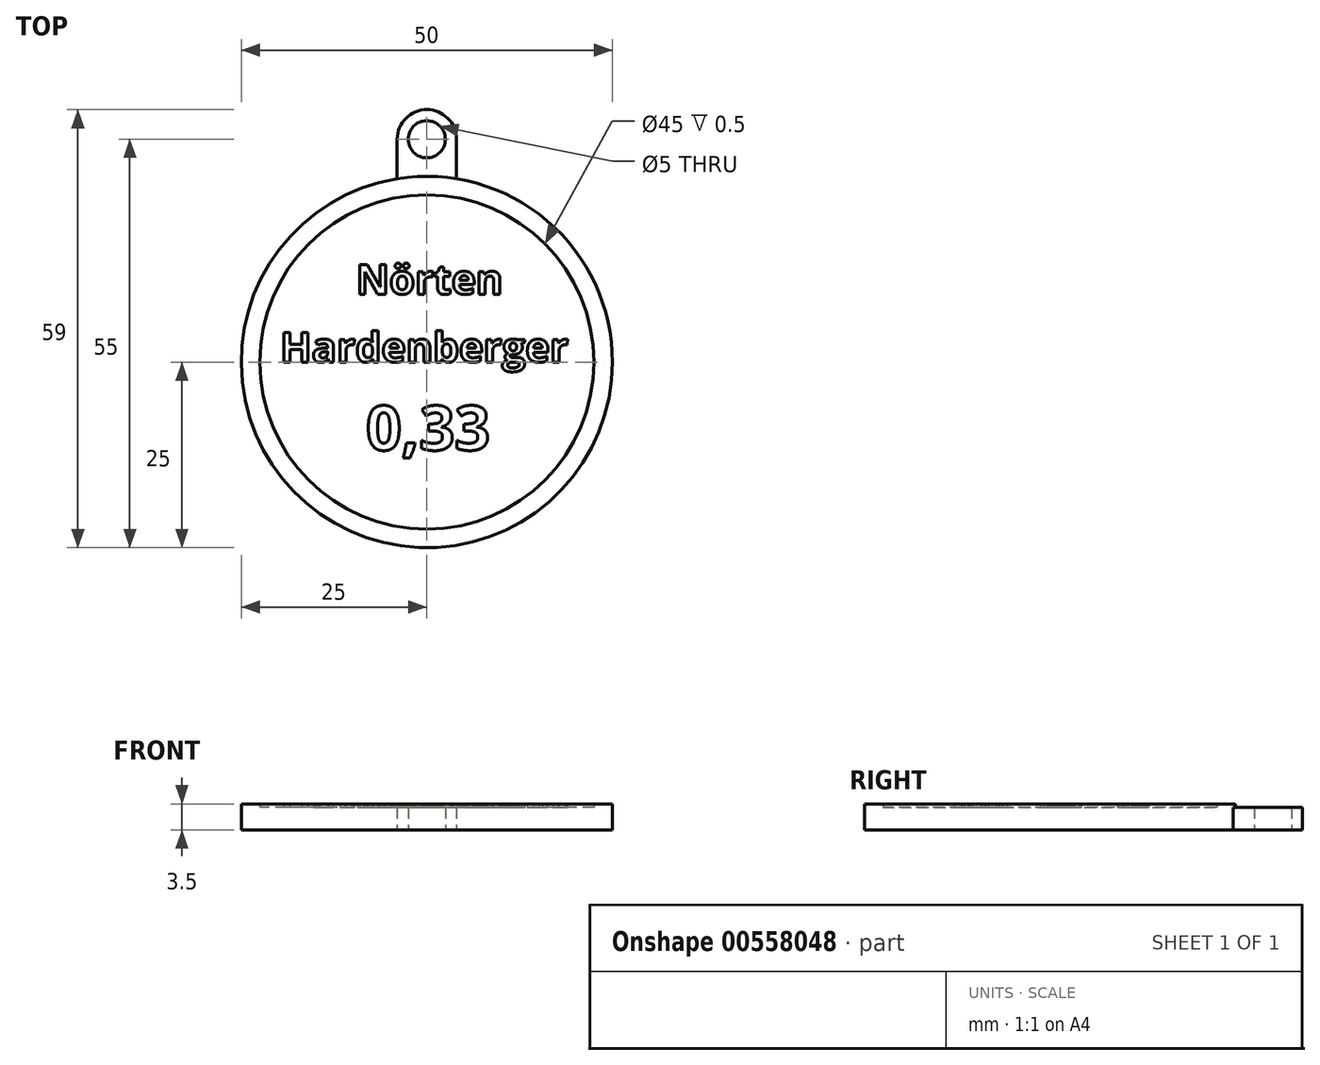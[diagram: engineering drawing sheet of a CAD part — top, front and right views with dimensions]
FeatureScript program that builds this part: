
annotation { "Feature Type Name" : "Feature", "Feature Type Description" : "" }
export const myFeature = defineFeature(function(context is Context, id is Id, definition is map)
    precondition{}
    {
        {
            var Q0;
            Q0=qCreatedBy(makeId("Top.planeOp"),FACE);
            var sketch = newSketch(context, id + "F0", { "sketchPlane" : qUnion([Q0])});
            skCircle(sketch, "E0", {"center": v(0, 0) * mm, "radius": 25 * mm});
            skCircle(sketch, "E1", {"center": v(0, 30) * mm, "radius": 2.5 * mm});
            skCircle(sketch, "E2", {"center": v(0, 30) * mm, "radius": 4 * mm});
            skLineSegment(sketch, "E3", {"start": v(-4, 30) * mm, "end": v(-4, 24.68) * mm});
            skLineSegment(sketch, "E4", {"start": v(4, 30) * mm, "end": v(4, 24.68) * mm});
            skCircle(sketch, "E5", {"center": v(0, 0) * mm, "radius": 22.5 * mm});
            skSolve(sketch);
        }
        {
            var Q0;
            {var subQ0=sQuery(id+"F0.wireOp",EDGE,"E0");var subQ1=makeQuery(id+"F0.imprint","INTERSECT",VERTEX,{"derivedFrom":[subQ0,sQuery(id+"F0.wireOp",EDGE,"E3")]});Q0=makeQuery(id+"F0.imprint","IMPRINT",FACE,{"disambiguationData":[TD([[makeQuery(id+"F0.imprint","IMPRINT",EDGE,{"disambiguationData":[TD([[subQ1,1.0]])],"derivedFrom":subQ0}),1.0]])]});}
            var Q1;
            {var subQ0=sQuery(id+"F0.wireOp",EDGE,"E3");Q1=makeQuery(id+"F0.imprint","IMPRINT",FACE,{"disambiguationData":[TD([[makeQuery(id+"F0.imprint","IMPRINT",EDGE,{"derivedFrom":subQ0}),1.0]])]});}
            var Q2;
            Q2=makeQuery(id+"F0.imprint","IMPRINT",FACE,{"disambiguationData":[TD([[makeQuery(id+"F0.imprint","IMPRINT",EDGE,{"derivedFrom":sQuery(id+"F0.wireOp",EDGE,"E1")}),-1.0]])]});
            var Q3;
            Q3=makeQuery(id+"F0.imprint","IMPRINT",FACE,{"disambiguationData":[TD([[makeQuery(id+"F0.imprint","IMPRINT",EDGE,{"derivedFrom":sQuery(id+"F0.wireOp",EDGE,"E5")}),1.0]])]});
            extrude(context, id + "F1", {"entities" : qUnion([Q0, Q1, Q2, Q3]), "depth" : 3 * mm, "offsetDistance" : 25 * mm});
        }
        {
            var Q0;
            Q0=makeQuery(id+"F1.opExtrude","CAP_FACE",FACE,{"disambiguationData":[OSD([sQuery(id+"F0.wireOp",EDGE,"E0"),sQuery(id+"F0.wireOp",EDGE,"E1"),sQuery(id+"F0.wireOp",EDGE,"E2"),sQuery(id+"F0.wireOp",EDGE,"E3"),sQuery(id+"F0.wireOp",EDGE,"E4")])],"isStart":false});
            var sketch = newSketch(context, id + "F2", { "sketchPlane" : qUnion([Q0])});
            skCircle(sketch, "E6", {"center": v(0, 0) * mm, "radius": 22.5 * mm});
            skText(sketch, "E7", { "text": "Nörten ", "fontName": "OpenSans-Bold.ttf"});
            skText(sketch, "E8", { "text": "Hardenberger", "fontName": "OpenSans-Bold.ttf"});
            skText(sketch, "E9", { "text": "0,33", "fontName": "OpenSans-Bold.ttf"});
            const initialGuessF2  = {"E7": [-0.00956, 0.00914, 1, 0, 0.004], "E8": [-0.01975, 0, 1, 0, 0.004], "E9": [-0.00818, -0.01186, 1, 0, 0.006]};
            skSetInitialGuess(sketch, initialGuessF2);
            skSolve(sketch);
        }
        {
            var Q0;
            Q0=makeQuery(id+"F2.imprint","IMPRINT",FACE,{"disambiguationData":[TD([[makeQuery(id+"F2.imprint","IMPRINT",EDGE,{"derivedFrom":sQuery(id+"F2.wireOp",EDGE,"E8.sketch_text.stroke-0")}),-1.0]])]});
            var Q1;
            Q1=makeQuery(id+"F2.imprint","IMPRINT",FACE,{"disambiguationData":[TD([[makeQuery(id+"F2.imprint","IMPRINT",EDGE,{"derivedFrom":sQuery(id+"F2.wireOp",EDGE,"E8.sketch_text.stroke-12")}),-1.0]])]});
            var Q2;
            Q2=makeQuery(id+"F2.imprint","IMPRINT",FACE,{"disambiguationData":[TD([[makeQuery(id+"F2.imprint","IMPRINT",EDGE,{"derivedFrom":sQuery(id+"F2.wireOp",EDGE,"E8.sketch_text.stroke-37")}),-1.0]])]});
            var Q3;
            Q3=makeQuery(id+"F2.imprint","IMPRINT",FACE,{"disambiguationData":[TD([[makeQuery(id+"F2.imprint","IMPRINT",EDGE,{"derivedFrom":sQuery(id+"F2.wireOp",EDGE,"E8.sketch_text.stroke-50")}),-1.0]])]});
            var Q4;
            Q4=makeQuery(id+"F2.imprint","IMPRINT",FACE,{"disambiguationData":[TD([[makeQuery(id+"F2.imprint","IMPRINT",EDGE,{"derivedFrom":sQuery(id+"F2.wireOp",EDGE,"E8.sketch_text.stroke-73")}),-1.0]])]});
            var Q5;
            Q5=makeQuery(id+"F2.imprint","IMPRINT",FACE,{"disambiguationData":[TD([[makeQuery(id+"F2.imprint","IMPRINT",EDGE,{"derivedFrom":sQuery(id+"F2.wireOp",EDGE,"E8.sketch_text.stroke-93")}),-1.0]])]});
            var Q6;
            Q6=makeQuery(id+"F2.imprint","IMPRINT",FACE,{"disambiguationData":[TD([[makeQuery(id+"F2.imprint","IMPRINT",EDGE,{"derivedFrom":sQuery(id+"F2.wireOp",EDGE,"E8.sketch_text.stroke-110")}),-1.0]])]});
            var Q7;
            Q7=makeQuery(id+"F2.imprint","IMPRINT",FACE,{"disambiguationData":[TD([[makeQuery(id+"F2.imprint","IMPRINT",EDGE,{"derivedFrom":sQuery(id+"F2.wireOp",EDGE,"E8.sketch_text.stroke-133")}),-1.0]])]});
            var Q8;
            Q8=makeQuery(id+"F2.imprint","IMPRINT",FACE,{"disambiguationData":[TD([[makeQuery(id+"F2.imprint","IMPRINT",EDGE,{"derivedFrom":sQuery(id+"F2.wireOp",EDGE,"E8.sketch_text.stroke-153")}),-1.0]])]});
            var Q9;
            Q9=makeQuery(id+"F2.imprint","IMPRINT",FACE,{"disambiguationData":[TD([[makeQuery(id+"F2.imprint","IMPRINT",EDGE,{"derivedFrom":sQuery(id+"F2.wireOp",EDGE,"E8.sketch_text.stroke-166")}),-1.0]])]});
            var Q10;
            Q10=makeQuery(id+"F2.imprint","IMPRINT",FACE,{"disambiguationData":[TD([[makeQuery(id+"F2.imprint","IMPRINT",EDGE,{"derivedFrom":sQuery(id+"F2.wireOp",EDGE,"E8.sketch_text.stroke-210")}),-1.0]])]});
            var Q11;
            Q11=makeQuery(id+"F2.imprint","IMPRINT",FACE,{"disambiguationData":[TD([[makeQuery(id+"F2.imprint","IMPRINT",EDGE,{"derivedFrom":sQuery(id+"F2.wireOp",EDGE,"E8.sketch_text.stroke-230")}),-1.0]])]});
            var Q12;
            Q12=makeQuery(id+"F2.imprint","IMPRINT",FACE,{"disambiguationData":[TD([[makeQuery(id+"F2.imprint","IMPRINT",EDGE,{"derivedFrom":sQuery(id+"F2.wireOp",EDGE,"E9.sketch_text.stroke-21")}),-1.0]])]});
            var Q13;
            Q13=makeQuery(id+"F2.imprint","IMPRINT",FACE,{"disambiguationData":[TD([[makeQuery(id+"F2.imprint","IMPRINT",EDGE,{"derivedFrom":sQuery(id+"F2.wireOp",EDGE,"E9.sketch_text.stroke-0")}),-1.0]])]});
            var Q14;
            Q14=makeQuery(id+"F2.imprint","IMPRINT",FACE,{"disambiguationData":[TD([[makeQuery(id+"F2.imprint","IMPRINT",EDGE,{"derivedFrom":sQuery(id+"F2.wireOp",EDGE,"E9.sketch_text.stroke-48")}),-1.0]])]});
            var Q15;
            Q15=makeQuery(id+"F2.imprint","IMPRINT",FACE,{"disambiguationData":[TD([[makeQuery(id+"F2.imprint","IMPRINT",EDGE,{"derivedFrom":sQuery(id+"F2.wireOp",EDGE,"E7.sketch_text.stroke-14")}),-1.0]])]});
            var Q16;
            Q16=makeQuery(id+"F2.imprint","IMPRINT",FACE,{"disambiguationData":[TD([[makeQuery(id+"F2.imprint","IMPRINT",EDGE,{"derivedFrom":sQuery(id+"F2.wireOp",EDGE,"E7.sketch_text.stroke-0")}),-1.0]])]});
            var Q17;
            Q17=makeQuery(id+"F2.imprint","IMPRINT",FACE,{"disambiguationData":[TD([[makeQuery(id+"F2.imprint","IMPRINT",EDGE,{"derivedFrom":sQuery(id+"F2.wireOp",EDGE,"E7.sketch_text.stroke-48")}),-1.0]])]});
            var Q18;
            Q18=makeQuery(id+"F2.imprint","IMPRINT",FACE,{"disambiguationData":[TD([[makeQuery(id+"F2.imprint","IMPRINT",EDGE,{"derivedFrom":sQuery(id+"F2.wireOp",EDGE,"E7.sketch_text.stroke-61")}),-1.0]])]});
            var Q19;
            Q19=makeQuery(id+"F2.imprint","IMPRINT",FACE,{"disambiguationData":[TD([[makeQuery(id+"F2.imprint","IMPRINT",EDGE,{"derivedFrom":sQuery(id+"F2.wireOp",EDGE,"E7.sketch_text.stroke-79")}),-1.0]])]});
            var Q20;
            Q20=makeQuery(id+"F2.imprint","IMPRINT",FACE,{"disambiguationData":[TD([[makeQuery(id+"F2.imprint","IMPRINT",EDGE,{"derivedFrom":sQuery(id+"F2.wireOp",EDGE,"E7.sketch_text.stroke-99")}),-1.0]])]});
            var Q21;
            Q21=makeQuery(id+"F2.imprint","IMPRINT",FACE,{"disambiguationData":[TD([[makeQuery(id+"F2.imprint","IMPRINT",EDGE,{"derivedFrom":sQuery(id+"F2.wireOp",EDGE,"E9.sketch_text.stroke-16")}),-1.0]])]});
            var Q22;
            Q22=makeQuery(id+"F2.imprint","IMPRINT",FACE,{"disambiguationData":[TD([[makeQuery(id+"F2.imprint","IMPRINT",EDGE,{"derivedFrom":sQuery(id+"F2.wireOp",EDGE,"E7.sketch_text.stroke-40")}),-1.0]])]});
            var Q23;
            Q23=makeQuery(id+"F2.imprint","IMPRINT",FACE,{"disambiguationData":[TD([[makeQuery(id+"F2.imprint","IMPRINT",EDGE,{"derivedFrom":sQuery(id+"F2.wireOp",EDGE,"E7.sketch_text.stroke-32")}),-1.0]])]});
            extrude(context, id + "F3", {"entities" : qUnion([Q0, Q1, Q2, Q3, Q4, Q5, Q6, Q7, Q8, Q9, Q10, Q11, Q12, Q13, Q14, Q15, Q16, Q17, Q18, Q19, Q20, Q21, Q22, Q23]), "operationType" : NewBodyOperationType.ADD, "depth" : 0.5 * mm, "offsetDistance" : 25 * mm});
        }
        {
            var Q0;
            {var subQ0=sQuery(id+"F0.wireOp",EDGE,"E2");var subQ1=sQuery(id+"F0.wireOp",EDGE,"E4");var subQ2=sQuery(id+"F0.wireOp",EDGE,"E0");var subQ3=sQuery(id+"F0.wireOp",EDGE,"E3");var subQ4=sQuery(id+"F0.wireOp",EDGE,"E1");Q0=makeQuery(id+"F3.boolean.opBoolean","SPLIT",FACE,{"disambiguationData":[TD([makeQuery(id+"F1.opExtrude","SWEPT_FACE",FACE,{"disambiguationData":[OSD([subQ2])]})])],"derivedFrom":makeQuery(id+"F1.opExtrude","CAP_FACE",FACE,{"disambiguationData":[OSD([subQ2,subQ4,subQ0,subQ3,subQ1])],"isStart":false})});}
            var sketch = newSketch(context, id + "F4", { "sketchPlane" : qUnion([Q0])});
            skCircle(sketch, "E10", {"center": v(0, 0) * mm, "radius": 25 * mm});
            skCircle(sketch, "E11", {"center": v(0, 0) * mm, "radius": 22.5 * mm});
            skSolve(sketch);
        }
        {
            var Q0;
            Q0=makeQuery(id+"F4.imprint","IMPRINT",FACE,{"disambiguationData":[TD([[makeQuery(id+"F4.imprint","IMPRINT",EDGE,{"derivedFrom":sQuery(id+"F4.wireOp",EDGE,"E11")}),-1.0]])]});
            extrude(context, id + "F5", {"entities" : qUnion([Q0]), "operationType" : NewBodyOperationType.ADD, "depth" : 0.5 * mm, "offsetDistance" : 25 * mm});
        }
    });
